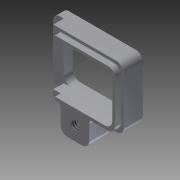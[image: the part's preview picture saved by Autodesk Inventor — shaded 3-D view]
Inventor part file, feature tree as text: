
AUTODESK INVENTOR PART (.ipt)
format: ipt  version: 2011 (Build 150239000, 239)  size: 183,296 bytes
history: native  units: in
note: dims shown in document units (in); Inventor stores cm internally (conversion verified against a paired STEP export)
features: sketch x7, extrude x6, fillet x1, hole x1
ambient origin geometry x8: Origin, YZ Plane, XZ Plane, XY Plane, X Axis, Y Axis, Z Axis, Center Point
bodies: Solid1 (feature_tree)
feature tree (15):
  extrude  "Extrusion1"  Depth=0.3543in
  extrude  "Extrusion2"  Depth=0.1378in
  extrude  "Extrusion3"  Depth=0.0315in
  extrude  "Extrusion4"  Depth=0.0315in
  fillet  "Fillet1"  Radius=0.1378in
  hole  "Hole2"  [1 undecoded]
  extrude  "Extrusion5"  Depth=0.0157in
  extrude  "Extrusion6"  Depth=0.1575in TaperAngle=0.0deg
  sketch  "Sketch1"  dims[d0=0.2756in d1=0.3543in]
  sketch  "Sketch2"  dims[d2=0.1772in d3=0.1378in]
  sketch  "Sketch3"  dims[d4=0.0591in d5=0.0315in]
  sketch  "Sketch4"  dims[d6=0.0315in d7=0.0315in d8=0.1378in d9=0.0in]
  sketch  "Sketch6"  dims[d10=0.0886in d11=0.0in d12=0.0157in]
  sketch  "Sketch7"  dims[d13=0.0157in d14=0.0157in]
  sketch  "Sketch8"  dims[d15=0.0315in d16=0.0in d19=0.1575in d20=0.0in d21=0.0394in d29=0.0394in d30=0.1575in d31=0.047in d32=0.75in d33=0.375in d34=0.25in d35=0.5635in d36=1.0in d37=0.8108in d38=0.0394in d39=0.0in d40=0.0394in d41=0.0in]
note: 1 required parameter value undecoded (feature->parameter linkage not recoverable at this tier; creation-order binding heuristic only, values carry confidence <= 0.55)
